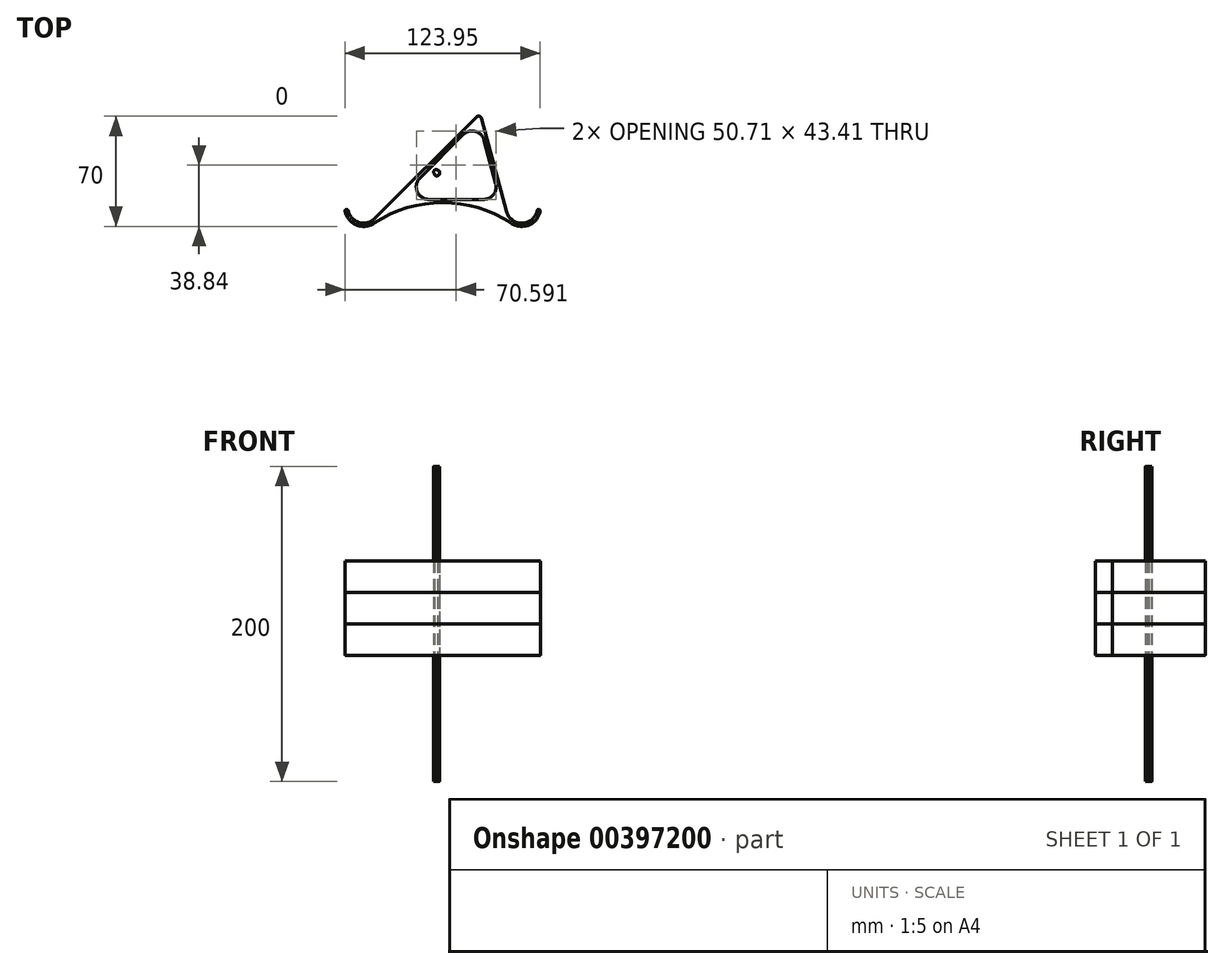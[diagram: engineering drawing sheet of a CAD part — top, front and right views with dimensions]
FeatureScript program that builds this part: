
annotation { "Feature Type Name" : "Feature", "Feature Type Description" : "" }
export const myFeature = defineFeature(function(context is Context, id is Id, definition is map)
    precondition{}
    {
        {
            var Q0;
            Q0=qCreatedBy(makeId("Top.planeOp"),FACE);
            var sketch = newSketch(context, id + "F0", { "sketchPlane" : qUnion([Q0])});
            skArc(sketch, "E0", {"start": v(-45.66, 8) * mm, "mid": v(-38.74, 0.42) * mm, "end": v(-28.8, 2.93) * mm});
            skArc(sketch, "E1.0", {"start": v(-47.62, 7.6) * mm, "mid": v(-39.32, -1.5) * mm, "end": v(-27.38, 1.51) * mm});
            skArc(sketch, "E2", {"start": v(-47.62, 7.6) * mm, "mid": v(-46.84, 8.78) * mm, "end": v(-45.66, 8) * mm});
            skArc(sketch, "E3.MirrorCS", {"start": v(76.3, 7.6) * mm, "mid": v(64.9, -2) * mm, "end": v(52.95, 6.9) * mm});
            skArc(sketch, "E4.MirrorCS", {"start": v(74.33, 8) * mm, "mid": v(64.84, 0) * mm, "end": v(54.88, 7.41) * mm});
            skLineSegment(sketch, "E5", {"start": v(-52.75, -2) * mm, "end": v(95.87, -2) * mm, "construction": true});
            skLineSegment(sketch, "E6", {"start": v(-28.8, 2.93) * mm, "end": v(35.7, 67.41) * mm});
            skLineSegment(sketch, "E7", {"start": v(54.88, 7.41) * mm, "end": v(39.04, 66.52) * mm});
            skLineSegment(sketch, "E8", {"start": v(52.95, 6.9) * mm, "end": v(40.7, 52.62) * mm});
            skLineSegment(sketch, "E9", {"start": v(-27.38, 1.51) * mm, "end": v(27.3, 56.2) * mm});
            skArc(sketch, "E10", {"start": v(74.33, 8) * mm, "mid": v(75.51, 8.78) * mm, "end": v(76.3, 7.6) * mm});
            skLineSegment(sketch, "E11", {"start": v(-7.94, 68) * mm, "end": v(55.98, 68) * mm, "construction": true});
            skArc(sketch, "E12", {"start": v(27.3, 56.2) * mm, "mid": v(35.04, 58.27) * mm, "end": v(40.7, 52.62) * mm});
            skArc(sketch, "E13", {"start": v(35.7, 67.41) * mm, "mid": v(37.63, 67.93) * mm, "end": v(39.04, 66.52) * mm});
            skArc(sketch, "E14", {"start": v(-0.1, 28.8) * mm, "mid": v(-1.83, 20.07) * mm, "end": v(5.56, 15.14) * mm});
            skArc(sketch, "E15", {"start": v(40.31, 15.14) * mm, "mid": v(46.66, 18.27) * mm, "end": v(48.04, 25.2) * mm});
            skArc(sketch, "E16", {"start": v(57.9, 0) * mm, "mid": v(14.34, 13.14) * mm, "end": v(-29.23, 0) * mm});
            skLineSegment(sketch, "E17", {"start": v(5.56, 15.14) * mm, "end": v(40.31, 15.14) * mm});
            skLineSegment(sketch, "E18", {"start": v(-34.41, 13.14) * mm, "end": v(67.53, 13.14) * mm, "construction": true});
            skLineSegment(sketch, "E19", {"start": v(5.56, 23.14) * mm, "end": v(32.97, 50.55) * mm, "construction": true});
            skLineSegment(sketch, "E20", {"start": v(40.31, 23.14) * mm, "end": v(5.56, 23.14) * mm, "construction": true});
            skLineSegment(sketch, "E21", {"start": v(32.97, 50.55) * mm, "end": v(40.31, 23.14) * mm, "construction": true});
            skLineSegment(sketch, "E22", {"start": v(5.56, 23.14) * mm, "end": v(36.64, 36.84) * mm, "construction": true});
            skLineSegment(sketch, "E23", {"start": v(36.64, 36.84) * mm, "end": v(40.31, 23.14) * mm, "construction": true});
            skLineSegment(sketch, "E24", {"start": v(40.31, 23.14) * mm, "end": v(19.26, 36.84) * mm, "construction": true});
            skLineSegment(sketch, "E25", {"start": v(19.26, 36.84) * mm, "end": v(32.97, 50.55) * mm, "construction": true});
            skLineSegment(sketch, "E26", {"start": v(32.97, 50.55) * mm, "end": v(22.93, 23.14) * mm, "construction": true});
            skLineSegment(sketch, "E27", {"start": v(26.28, 32.27) * mm, "end": v(26.28, 43.86) * mm, "construction": true});
            skSolve(sketch);
        }
        {
            var Q0;
            {var subQ3=sQuery(id+"F0.wireOp",EDGE,"E14");Q0=makeQuery(id+"F0.imprint","IMPRINT",FACE,{"disambiguationData":[TD([[makeQuery(id+"F0.imprint","IMPRINT",EDGE,{"derivedFrom":subQ3}),-1.0]])]});}
            var Q1;
            {var subQ5=sQuery(id+"F0.wireOp",EDGE,"E15");Q1=makeQuery(id+"F0.imprint","IMPRINT",FACE,{"disambiguationData":[TD([[makeQuery(id+"F0.imprint","IMPRINT",EDGE,{"derivedFrom":subQ5}),-1.0]])]});}
            var Q2;
            Q2=makeQuery(id+"F0.imprint","IMPRINT",FACE,{"disambiguationData":[TD([[makeQuery(id+"F0.imprint","IMPRINT",EDGE,{"derivedFrom":sQuery(id+"F0.wireOp",EDGE,"E0")}),-1.0]])]});
            extrude(context, id + "F1", {"entities" : qUnion([Q0, Q1, Q2]), "depth" : 40 * mm});
        }
        {
            var Q0;
            Q0=qCreatedBy(makeId("Top.planeOp"),FACE);
            var sketch = newSketch(context, id + "F2", { "sketchPlane" : qUnion([Q0])});
            skLineSegment(sketch, "E28.MirrorCS", {"start": v(6.62, 25.43) * mm, "end": v(6.62, 25.43) * mm});
            skLineSegment(sketch, "E29.MirrorCS", {"start": v(48.04, 35.28) * mm, "end": v(48.18, 35.73) * mm});
            skLineSegment(sketch, "E30.MirrorCS", {"start": v(49.9, 35.51) * mm, "end": v(50.43, 35.53) * mm});
            skFitSpline(sketch, "E31.MirrorCS", {"points": [v(50.57, 35.24) * mm, v(50.73, 34.92) * mm, v(50.74, 34.93) * mm, v(49.87, 34.77) * mm]});
            skLineSegment(sketch, "E32.MirrorCS", {"start": v(48.18, 35.73) * mm, "end": v(48.77, 35.62) * mm});
            skFitSpline(sketch, "E33.MirrorCS", {"points": [v(48.77, 35.62) * mm, v(49.1, 35.55) * mm, v(49.6, 35.5) * mm, v(49.9, 35.51) * mm]});
            skFitSpline(sketch, "E34.MirrorCS", {"points": [v(49.87, 34.77) * mm, v(49.4, 34.68) * mm, v(48.44, 34.7) * mm, v(48.06, 34.8) * mm]});
            skLineSegment(sketch, "E35.MirrorCS", {"start": v(45.66, 35.67) * mm, "end": v(46.15, 36.02) * mm});
            skLineSegment(sketch, "E36.MirrorCS", {"start": v(50.57, 35.24) * mm, "end": v(49.9, 35.51) * mm});
            skLineSegment(sketch, "E37.MirrorCS", {"start": v(48.77, 35.62) * mm, "end": v(48.04, 35.28) * mm});
            skLineSegment(sketch, "E38.MirrorCS", {"start": v(24.83, 34) * mm, "end": v(25.27, 33.6) * mm});
            skFitSpline(sketch, "E39.MirrorCS", {"points": [v(48.06, 34.8) * mm, v(47.93, 34.83) * mm, v(47.92, 34.91) * mm, v(48.04, 35.28) * mm]});
            skLineSegment(sketch, "E40.MirrorCS", {"start": v(50.43, 35.53) * mm, "end": v(50.57, 35.24) * mm});
            skLineSegment(sketch, "E41.MirrorCS", {"start": v(24.04, 33.1) * mm, "end": v(24.83, 34) * mm});
            skLineSegment(sketch, "E42.MirrorCS", {"start": v(27.95, 36.55) * mm, "end": v(27.5, 36.98) * mm});
            skLineSegment(sketch, "E43.MirrorCS", {"start": v(25.27, 33.6) * mm, "end": v(24.04, 33.1) * mm});
            skFitSpline(sketch, "E44.MirrorCS", {"points": [v(23.48, 31.83) * mm, v(23.32, 31.94) * mm, v(23.2, 32.08) * mm, v(23.22, 32.13) * mm]});
            skLineSegment(sketch, "E45.MirrorCS", {"start": v(45.99, 35.5) * mm, "end": v(45.66, 35.67) * mm});
            skFitSpline(sketch, "E46.MirrorCS", {"points": [v(9.41, 22.4) * mm, v(9.04, 22.05) * mm, v(8.66, 21.27) * mm, v(9.25, 20.95) * mm]});
            skFitSpline(sketch, "E47.MirrorCS", {"points": [v(42.3, 51.5) * mm, v(42.77, 51.58) * mm, v(43.01, 51.72) * mm, v(43.32, 52.05) * mm]});
            skFitSpline(sketch, "E48.MirrorCS", {"points": [v(31.88, 38.91) * mm, v(32.18, 39.25) * mm, v(32.3, 39.6) * mm, v(32.25, 40.03) * mm]});
            skFitSpline(sketch, "E49.MirrorCS", {"points": [v(30.97, 38.42) * mm, v(31.39, 38.5) * mm, v(31.6, 38.61) * mm, v(31.88, 38.91) * mm]});
            skFitSpline(sketch, "E50.MirrorCS", {"points": [v(23.05, 28.46) * mm, v(23.58, 28.75) * mm, v(24.07, 29.32) * mm, v(24.23, 29.83) * mm]});
            skFitSpline(sketch, "E51.MirrorCS", {"points": [v(26.76, 36.62) * mm, v(25.59, 36.98) * mm, v(24.53, 35.93) * mm, v(24.88, 34.73) * mm]});
            skFitSpline(sketch, "E52.MirrorCS", {"points": [v(28.34, 41.94) * mm, v(28.27, 41.8) * mm, v(28.2, 41.48) * mm, v(28.2, 41.21) * mm]});
            skLineSegment(sketch, "E53.MirrorCS", {"start": v(28.2, 40.72) * mm, "end": v(27.2, 39.57) * mm});
            skFitSpline(sketch, "E54.MirrorCS", {"points": [v(23.22, 32.13) * mm, v(23.24, 32.18) * mm, v(23.6, 32.62) * mm, v(24.04, 33.1) * mm]});
            skFitSpline(sketch, "E55.MirrorCS", {"points": [v(43.74, 53.32) * mm, v(43.67, 54.09) * mm, v(43.26, 54.6) * mm, v(42.55, 54.83) * mm]});
            skLineSegment(sketch, "E56.MirrorCS", {"start": v(27.2, 39.57) * mm, "end": v(28.2, 41.21) * mm});
            skLineSegment(sketch, "E57.MirrorCS", {"start": v(19.54, 31.48) * mm, "end": v(19.54, 30.95) * mm});
            skFitSpline(sketch, "E58.MirrorCS", {"points": [v(4.92, 38.14) * mm, v(5.34, 37.8) * mm, v(5.74, 37.41) * mm, v(5.81, 37.27) * mm]});
            skFitSpline(sketch, "E59.MirrorCS", {"points": [v(43.32, 52.05) * mm, v(43.66, 52.43) * mm, v(43.79, 52.83) * mm, v(43.74, 53.32) * mm]});
            skLineSegment(sketch, "E60.MirrorCS", {"start": v(28.2, 41.21) * mm, "end": v(28.2, 40.72) * mm});
            skFitSpline(sketch, "E61.MirrorCS", {"points": [v(22.21, 28.9) * mm, v(22.63, 28.97) * mm, v(22.84, 29.1) * mm, v(23.11, 29.4) * mm]});
            skLineSegment(sketch, "E62.MirrorCS", {"start": v(46.15, 36.02) * mm, "end": v(45.99, 35.5) * mm});
            skFitSpline(sketch, "E63.MirrorCS", {"points": [v(24.08, 37.14) * mm, v(23.93, 36.95) * mm, v(23.9, 36.8) * mm, v(23.9, 36.38) * mm]});
            skLineSegment(sketch, "E64.MirrorCS", {"start": v(22.89, 34.72) * mm, "end": v(23.9, 36.38) * mm});
            skLineSegment(sketch, "E65.MirrorCS", {"start": v(23.9, 36.38) * mm, "end": v(23.9, 35.86) * mm});
            skFitSpline(sketch, "E66.MirrorCS", {"points": [v(27.82, 40.9) * mm, v(27.75, 41.6) * mm, v(27.96, 42.45) * mm, v(28.7, 42.7) * mm]});
            skFitSpline(sketch, "E67.MirrorCS", {"points": [v(23.5, 30.51) * mm, v(23.43, 31.19) * mm, v(23.06, 31.65) * mm, v(22.43, 31.84) * mm]});
            skFitSpline(sketch, "E68.MirrorCS", {"points": [v(29.54, 42.54) * mm, v(29.08, 42.5) * mm, v(28.5, 42.2) * mm, v(28.34, 41.94) * mm]});
            skFitSpline(sketch, "E69.MirrorCS", {"points": [v(27.82, 35.29) * mm, v(27.76, 35.96) * mm, v(27.4, 36.42) * mm, v(26.76, 36.62) * mm]});
            skFitSpline(sketch, "E70.MirrorCS", {"points": [v(29.3, 39.47) * mm, v(29.5, 38.8) * mm, v(30.3, 38.3) * mm, v(30.97, 38.42) * mm]});
            skFitSpline(sketch, "E71.MirrorCS", {"points": [v(20.85, 32.83) * mm, v(19.99, 32.81) * mm, v(19.54, 32.35) * mm, v(19.54, 31.48) * mm]});
            skFitSpline(sketch, "E72.MirrorCS", {"points": [v(23.11, 29.4) * mm, v(23.41, 29.72) * mm, v(23.53, 30.08) * mm, v(23.5, 30.51) * mm]});
            skLineSegment(sketch, "E73.MirrorCS", {"start": v(27.5, 36.98) * mm, "end": v(28.26, 37.85) * mm});
            skFitSpline(sketch, "E74.MirrorCS", {"points": [v(22.89, 34.72) * mm, v(21.25, 32.86) * mm, v(21.22, 32.83) * mm, v(20.85, 32.83) * mm]});
            skFitSpline(sketch, "E75.MirrorCS", {"points": [v(46.22, 36.57) * mm, v(46.27, 36.55) * mm, v(46.24, 36.3) * mm, v(46.15, 36.02) * mm]});
            skFitSpline(sketch, "E76.MirrorCS", {"points": [v(19.15, 31.08) * mm, v(19.01, 31.98) * mm, v(19.48, 33.12) * mm, v(20.5, 33.17) * mm]});
            skFitSpline(sketch, "E77.MirrorCS", {"points": [v(53.13, 34.93) * mm, v(53.33, 34.16) * mm, v(52.73, 33.5) * mm, v(52.1, 33.16) * mm]});
            skLineSegment(sketch, "E78.MirrorCS", {"start": v(23.9, 35.86) * mm, "end": v(22.89, 34.72) * mm});
            skFitSpline(sketch, "E79.MirrorCS", {"points": [v(29.12, 38.78) * mm, v(29.18, 38.8) * mm, v(29.36, 38.7) * mm, v(29.52, 38.54) * mm]});
            skFitSpline(sketch, "E80.MirrorCS", {"points": [v(10.22, 20.85) * mm, v(9.4, 20.35) * mm, v(8.88, 20.44) * mm, v(8.6, 21.14) * mm]});
            skLineSegment(sketch, "E81.MirrorCS", {"start": v(28.26, 37.85) * mm, "end": v(27.95, 36.55) * mm});
            skFitSpline(sketch, "E82.MirrorCS", {"points": [v(28.26, 37.85) * mm, v(28.68, 38.33) * mm, v(29.07, 38.75) * mm, v(29.12, 38.78) * mm]});
            skFitSpline(sketch, "E83.MirrorCS", {"points": [v(22.43, 31.84) * mm, v(21.25, 32.2) * mm, v(20.2, 31.15) * mm, v(20.54, 29.95) * mm]});
            skFitSpline(sketch, "E84.MirrorCS", {"points": [v(32.25, 40.03) * mm, v(32.19, 40.71) * mm, v(31.82, 41.17) * mm, v(31.2, 41.36) * mm]});
            skFitSpline(sketch, "E85.MirrorCS", {"points": [v(5.76, 40.05) * mm, v(5.8, 40.08) * mm, v(6.57, 40.09) * mm, v(7.46, 40.07) * mm]});
            skFitSpline(sketch, "E86.MirrorCS", {"points": [v(24.23, 29.83) * mm, v(24.42, 30.47) * mm, v(24.09, 31.37) * mm, v(23.48, 31.83) * mm]});
            skFitSpline(sketch, "E87.MirrorCS", {"points": [v(6.18, 39.61) * mm, v(5.9, 39.83) * mm, v(5.7, 40.02) * mm, v(5.76, 40.05) * mm]});
            skFitSpline(sketch, "E88.MirrorCS", {"points": [v(24.88, 34.73) * mm, v(25.07, 34.06) * mm, v(25.88, 33.55) * mm, v(26.54, 33.67) * mm]});
            skFitSpline(sketch, "E89.MirrorCS", {"points": [v(27.2, 39.57) * mm, v(25.6, 37.77) * mm, v(25.5, 37.68) * mm, v(25.11, 37.67) * mm]});
            skFitSpline(sketch, "E90.MirrorCS", {"points": [v(32.14, 41.57) * mm, v(31.95, 41.73) * mm, v(31.82, 41.89) * mm, v(31.86, 41.92) * mm]});
            skFitSpline(sketch, "E91.MirrorCS", {"points": [v(20.43, 29) * mm, v(20.52, 29.09) * mm, v(20.6, 29.05) * mm, v(20.84, 28.82) * mm]});
            skFitSpline(sketch, "E92.MirrorCS", {"points": [v(31.2, 41.36) * mm, v(30.02, 41.73) * mm, v(28.96, 40.67) * mm, v(29.3, 39.47) * mm]});
            skFitSpline(sketch, "E93.MirrorCS", {"points": [v(22, 34.29) * mm, v(22.49, 34.87) * mm, v(23.05, 35.44) * mm, v(23.5, 36.04) * mm]});
            skFitSpline(sketch, "E94.MirrorCS", {"points": [v(52.54, 34.03) * mm, v(52.9, 34.47) * mm, v(52.88, 34.61) * mm, v(52.39, 35.88) * mm]});
            skFitSpline(sketch, "E95.MirrorCS", {"points": [v(3.58, 40.91) * mm, v(3.44, 40.63) * mm, v(3.42, 40.46) * mm, v(3.49, 40.06) * mm]});
            skFitSpline(sketch, "E96.MirrorCS", {"points": [v(3.49, 40.06) * mm, v(3.6, 39.4) * mm, v(4, 38.87) * mm, v(4.92, 38.14) * mm]});
            skFitSpline(sketch, "E97.MirrorCS", {"points": [v(28.52, 34.7) * mm, v(28.68, 35.22) * mm, v(28.68, 35.36) * mm, v(28.55, 35.72) * mm]});
            skFitSpline(sketch, "E98.MirrorCS", {"points": [v(28.55, 35.72) * mm, v(28.47, 35.95) * mm, v(28.21, 36.3) * mm, v(27.95, 36.55) * mm]});
            skFitSpline(sketch, "E99.MirrorCS", {"points": [v(25.69, 38.48) * mm, v(26.41, 39.27) * mm, v(27.16, 40.08) * mm, v(27.82, 40.9) * mm]});
            skFitSpline(sketch, "E100.MirrorCS", {"points": [v(20.5, 33.17) * mm, v(21.24, 33.1) * mm, v(21.53, 33.88) * mm, v(22, 34.29) * mm]});
            skFitSpline(sketch, "E101.MirrorCS", {"points": [v(5.06, 37.51) * mm, v(4.2, 38.24) * mm, v(3.1, 39.04) * mm, v(3.06, 40.28) * mm]});
            skFitSpline(sketch, "E102.MirrorCS", {"points": [v(48.78, 32.8) * mm, v(50.3, 32.7) * mm, v(51.92, 33.24) * mm, v(52.54, 34.03) * mm]});
            skFitSpline(sketch, "E103.MirrorCS", {"points": [v(44.95, 33.86) * mm, v(45.76, 33.42) * mm, v(47.79, 32.85) * mm, v(48.78, 32.8) * mm]});
            skFitSpline(sketch, "E104.MirrorCS", {"points": [v(40.4, 41.91) * mm, v(40.43, 41.9) * mm, v(40.56, 41.37) * mm, v(40.69, 40.73) * mm]});
            skFitSpline(sketch, "E105.MirrorCS", {"points": [v(40.4, 55.54) * mm, v(41.14, 56.15) * mm, v(42.13, 56.4) * mm, v(43, 56.12) * mm]});
            skFitSpline(sketch, "E106.MirrorCS", {"points": [v(44.8, 47.35) * mm, v(44.32, 49.01) * mm, v(43.4, 50.3) * mm, v(42.18, 50.97) * mm]});
            skFitSpline(sketch, "E107.MirrorCS", {"points": [v(45.58, 43.37) * mm, v(45.28, 45.13) * mm, v(44.93, 46.92) * mm, v(44.8, 47.35) * mm]});
            skFitSpline(sketch, "E108.MirrorCS", {"points": [v(25.11, 37.67) * mm, v(24.71, 37.67) * mm, v(24.34, 37.47) * mm, v(24.08, 37.14) * mm]});
            skFitSpline(sketch, "E109.MirrorCS", {"points": [v(20.38, 37.88) * mm, v(21.86, 38.76) * mm, v(22.27, 39.13) * mm, v(22.47, 39.77) * mm]});
            skFitSpline(sketch, "E110.MirrorCS", {"points": [v(41.42, 37.18) * mm, v(40.8, 38.4) * mm, v(40.46, 39.87) * mm, v(40.18, 41.1) * mm]});
            skFitSpline(sketch, "E111.MirrorCS", {"points": [v(39.23, 53.73) * mm, v(39.43, 54.38) * mm, v(39.84, 55.08) * mm, v(40.4, 55.54) * mm]});
            skFitSpline(sketch, "E112.MirrorCS", {"points": [v(7.88, 37.1) * mm, v(7.7, 38.16) * mm, v(7.28, 38.78) * mm, v(6.18, 39.61) * mm]});
            skFitSpline(sketch, "E113.MirrorCS", {"points": [v(20.84, 28.82) * mm, v(21.55, 28.13) * mm, v(22.26, 28.02) * mm, v(23.05, 28.46) * mm]});
            skFitSpline(sketch, "E114.MirrorCS", {"points": [v(17.8, 33.88) * mm, v(18.86, 36.74) * mm, v(19.1, 37.11) * mm, v(20.38, 37.88) * mm]});
            skFitSpline(sketch, "E115.MirrorCS", {"points": [v(39.39, 51.6) * mm, v(39.07, 52.27) * mm, v(39.01, 53.03) * mm, v(39.23, 53.73) * mm]});
            skFitSpline(sketch, "E116.MirrorCS", {"points": [v(19.37, 18.24) * mm, v(19.01, 17.77) * mm, v(18.31, 16.96) * mm, v(17.82, 16.45) * mm]});
            skFitSpline(sketch, "E117.MirrorCS", {"points": [v(22.62, 39.19) * mm, v(21.76, 37.77) * mm, v(19.66, 37.59) * mm, v(19.06, 35.94) * mm]});
            skFitSpline(sketch, "E118.MirrorCS", {"points": [v(0.36, 15) * mm, v(1.45, 13.37) * mm, v(2.47, 12.45) * mm, v(4.04, 11.65) * mm]});
            skFitSpline(sketch, "E119.MirrorCS", {"points": [v(10.96, 30.2) * mm, v(11.44, 30.3) * mm, v(11.7, 30.43) * mm, v(12, 30.78) * mm]});
            skFitSpline(sketch, "E120.MirrorCS", {"points": [v(17.64, 40.03) * mm, v(18.97, 40.04) * mm, v(20.07, 40.02) * mm, v(20.09, 40) * mm]});
            skFitSpline(sketch, "E121.MirrorCS", {"points": [v(40.69, 40.73) * mm, v(40.98, 39.23) * mm, v(41.28, 38.33) * mm, v(41.86, 37.18) * mm]});
            skFitSpline(sketch, "E122.MirrorCS", {"points": [v(2.49, 12.14) * mm, v(0.56, 13.59) * mm, v(-0.73, 15.73) * mm, v(-1.63, 17.93) * mm]});
            skFitSpline(sketch, "E123.MirrorCS", {"points": [v(19.56, 15.48) * mm, v(19.97, 15.92) * mm, v(21.03, 17.22) * mm, v(21.9, 18.36) * mm]});
            skFitSpline(sketch, "E124.MirrorCS", {"points": [v(5.58, 35.66) * mm, v(5.62, 36.31) * mm, v(5.67, 37.1) * mm, v(5.06, 37.51) * mm]});
            skFitSpline(sketch, "E125.MirrorCS", {"points": [v(6.62, 25.43) * mm, v(8.06, 25.42) * mm, v(8.9, 27.19) * mm, v(8, 28.3) * mm]});
            skFitSpline(sketch, "E126.MirrorCS", {"points": [v(4.75, 13.44) * mm, v(3.58, 14.04) * mm, v(2.93, 14.64) * mm, v(2.1, 15.87) * mm]});
            skFitSpline(sketch, "E127.MirrorCS", {"points": [v(9.02, 31.43) * mm, v(9.25, 30.66) * mm, v(10.18, 30.06) * mm, v(10.96, 30.2) * mm]});
            skFitSpline(sketch, "E128.MirrorCS", {"points": [v(43.53, 50.41) * mm, v(44.57, 49.35) * mm, v(45.18, 47.85) * mm, v(45.41, 46.4) * mm]});
            skFitSpline(sketch, "E129.MirrorCS", {"points": [v(5, 41.9) * mm, v(4.38, 41.79) * mm, v(3.82, 41.4) * mm, v(3.58, 40.91) * mm]});
            skFitSpline(sketch, "E130.MirrorCS", {"points": [v(40.23, 41.78) * mm, v(40.29, 41.87) * mm, v(40.36, 41.92) * mm, v(40.4, 41.91) * mm]});
            skFitSpline(sketch, "E131.MirrorCS", {"points": [v(24.55, 37.96) * mm, v(24.97, 38.05) * mm, v(25.45, 38.05) * mm, v(25.69, 38.48) * mm]});
            skFitSpline(sketch, "E132.MirrorCS", {"points": [v(39.56, 51.24) * mm, v(38.85, 51.13) * mm, v(38.46, 51) * mm, v(37.69, 50.59) * mm]});
            skFitSpline(sketch, "E133.MirrorCS", {"points": [v(20.09, 40) * mm, v(20.1, 39.97) * mm, v(19.75, 39.74) * mm, v(19.31, 39.48) * mm]});
            skFitSpline(sketch, "E134.MirrorCS", {"points": [v(12, 30.78) * mm, v(12.36, 31.17) * mm, v(12.5, 31.58) * mm, v(12.45, 32.08) * mm]});
            skFitSpline(sketch, "E135.MirrorCS", {"points": [v(25.27, 33.6) * mm, v(26.44, 32.56) * mm, v(28.02, 33.09) * mm, v(28.52, 34.7) * mm]});
            skFitSpline(sketch, "E136.MirrorCS", {"points": [v(44.98, 37.99) * mm, v(45.34, 37.35) * mm, v(45.95, 36.65) * mm, v(46.22, 36.57) * mm]});
            skFitSpline(sketch, "E137.MirrorCS", {"points": [v(23.5, 36.04) * mm, v(23.38, 36.82) * mm, v(23.74, 37.72) * mm, v(24.55, 37.96) * mm]});
            skFitSpline(sketch, "E138.MirrorCS", {"points": [v(21.83, 41.95) * mm, v(22.87, 41.5) * mm, v(23.25, 40.12) * mm, v(22.62, 39.19) * mm]});
            skFitSpline(sketch, "E139.MirrorCS", {"points": [v(40.41, 52.69) * mm, v(40.63, 51.94) * mm, v(41.54, 51.36) * mm, v(42.3, 51.5) * mm]});
            skFitSpline(sketch, "E140.MirrorCS", {"points": [v(-1.58, 21.03) * mm, v(-1.78, 19) * mm, v(-1.27, 17.42) * mm, v(0.36, 15) * mm]});
            skFitSpline(sketch, "E141.MirrorCS", {"points": [v(52.39, 35.88) * mm, v(51.8, 37.4) * mm, v(51.51, 37.66) * mm, v(50.65, 37.51) * mm]});
            skFitSpline(sketch, "E142.MirrorCS", {"points": [v(50.65, 37.51) * mm, v(49.94, 37.4) * mm, v(48.97, 37.5) * mm, v(48.11, 37.82) * mm]});
            skFitSpline(sketch, "E143.MirrorCS", {"points": [v(22.47, 39.77) * mm, v(22.7, 40.54) * mm, v(22.36, 41.27) * mm, v(21.59, 41.65) * mm]});
            skFitSpline(sketch, "E144.MirrorCS", {"points": [v(9.25, 20.95) * mm, v(10.07, 20.9) * mm, v(10.63, 21.73) * mm, v(11.18, 22.22) * mm]});
            skFitSpline(sketch, "E145.MirrorCS", {"points": [v(44.8, 54.16) * mm, v(45.03, 53.45) * mm, v(44.98, 52.68) * mm, v(44.77, 52) * mm]});
            skFitSpline(sketch, "E146.MirrorCS", {"points": [v(12.45, 32.08) * mm, v(12.37, 32.87) * mm, v(11.95, 33.4) * mm, v(11.22, 33.63) * mm]});
            skFitSpline(sketch, "E147.MirrorCS", {"points": [v(42.55, 54.83) * mm, v(41.22, 55.24) * mm, v(40.02, 54.04) * mm, v(40.41, 52.69) * mm]});
            skFitSpline(sketch, "E148.MirrorCS", {"points": [v(49.98, 37.84) * mm, v(50.69, 37.93) * mm, v(51.59, 38.1) * mm, v(52.05, 37.4) * mm]});
            skFitSpline(sketch, "E149.MirrorCS", {"points": [v(3.06, 40.28) * mm, v(3.02, 41.5) * mm, v(4.26, 42.3) * mm, v(5.37, 42.33) * mm]});
            skFitSpline(sketch, "E150.MirrorCS", {"points": [v(5.13, 28.15) * mm, v(4.87, 27.76) * mm, v(4.87, 27.73) * mm, v(4.85, 27.27) * mm]});
            skFitSpline(sketch, "E151.MirrorCS", {"points": [v(6.64, 21.04) * mm, v(6.77, 20.22) * mm, v(7.13, 19.6) * mm, v(7.76, 19.11) * mm]});
            skFitSpline(sketch, "E152.MirrorCS", {"points": [v(37.69, 50.59) * mm, v(36.8, 50.11) * mm, v(36.62, 49.97) * mm, v(35.44, 48.75) * mm]});
            skFitSpline(sketch, "E153.MirrorCS", {"points": [v(20.54, 29.95) * mm, v(20.74, 29.29) * mm, v(21.54, 28.77) * mm, v(22.21, 28.9) * mm]});
            skFitSpline(sketch, "E154.MirrorCS", {"points": [v(6.83, 22.51) * mm, v(6.55, 21.76) * mm, v(6.54, 21.68) * mm, v(6.64, 21.04) * mm]});
            skFitSpline(sketch, "E155.MirrorCS", {"points": [v(45.66, 35.67) * mm, v(45.06, 35.96) * mm, v(44.21, 36.87) * mm, v(43.73, 37.73) * mm]});
            skFitSpline(sketch, "E156.MirrorCS", {"points": [v(42.18, 50.97) * mm, v(41.52, 51.34) * mm, v(40.74, 51.42) * mm, v(39.56, 51.24) * mm]});
            skFitSpline(sketch, "E157.MirrorCS", {"points": [v(41.63, 44.26) * mm, v(41.04, 44.83) * mm, v(40.1, 44.66) * mm, v(39.41, 43.86) * mm]});
            skFitSpline(sketch, "E158.MirrorCS", {"points": [v(28.7, 42.7) * mm, v(29.16, 42.9) * mm, v(29.75, 42.87) * mm, v(30.01, 43.37) * mm]});
            skFitSpline(sketch, "E159.MirrorCS", {"points": [v(0.7, 22.62) * mm, v(1.06, 23.9) * mm, v(1.15, 24.14) * mm, v(1.54, 24.78) * mm]});
            skFitSpline(sketch, "E160.MirrorCS", {"points": [v(4.85, 27.27) * mm, v(4.82, 26.3) * mm, v(5.64, 25.44) * mm, v(6.62, 25.43) * mm]});
            skFitSpline(sketch, "E161.MirrorCS", {"points": [v(8.6, 21.14) * mm, v(8.35, 21.82) * mm, v(8.8, 22.49) * mm, v(10.64, 24.14) * mm]});
            skFitSpline(sketch, "E162.MirrorCS", {"points": [v(42.5, 41.56) * mm, v(42.13, 43.55) * mm, v(42.03, 43.87) * mm, v(41.63, 44.26) * mm]});
            skFitSpline(sketch, "E163.MirrorCS", {"points": [v(8, 28.3) * mm, v(7.24, 29.23) * mm, v(5.77, 29.15) * mm, v(5.13, 28.15) * mm]});
            skFitSpline(sketch, "E164.MirrorCS", {"points": [v(5.81, 37.27) * mm, v(6.1, 36.7) * mm, v(6.03, 35.3) * mm, v(5.66, 34.13) * mm]});
            skFitSpline(sketch, "E165.MirrorCS", {"points": [v(47, 39.1) * mm, v(47.64, 38.12) * mm, v(48.92, 37.93) * mm, v(49.98, 37.84) * mm]});
            skFitSpline(sketch, "E166.MirrorCS", {"points": [v(32.4, 38.69) * mm, v(33.24, 39.62) * mm, v(33.15, 40.69) * mm, v(32.14, 41.57) * mm]});
            skFitSpline(sketch, "E167.MirrorCS", {"points": [v(29.52, 38.54) * mm, v(30.44, 37.64) * mm, v(31.49, 37.7) * mm, v(32.4, 38.69) * mm]});
            skFitSpline(sketch, "E168.MirrorCS", {"points": [v(27.45, 34.17) * mm, v(27.75, 34.5) * mm, v(27.87, 34.85) * mm, v(27.82, 35.29) * mm]});
            skFitSpline(sketch, "E169.MirrorCS", {"points": [v(32.01, 45) * mm, v(30.08, 42.82) * mm, v(29.82, 42.56) * mm, v(29.54, 42.54) * mm]});
            skFitSpline(sketch, "E170.MirrorCS", {"points": [v(26.54, 33.67) * mm, v(26.96, 33.75) * mm, v(27.18, 33.87) * mm, v(27.45, 34.17) * mm]});
            skFitSpline(sketch, "E171.MirrorCS", {"points": [v(44.77, 52) * mm, v(44.56, 51.35) * mm, v(44.12, 50.78) * mm, v(43.53, 50.41) * mm]});
            skFitSpline(sketch, "E172.MirrorCS", {"points": [v(52.05, 37.4) * mm, v(52.6, 36.68) * mm, v(52.82, 35.77) * mm, v(53.13, 34.93) * mm]});
            skFitSpline(sketch, "E173.MirrorCS", {"points": [v(43, 56.12) * mm, v(43.86, 55.85) * mm, v(44.53, 55.06) * mm, v(44.8, 54.16) * mm]});
            skFitSpline(sketch, "E174.MirrorCS", {"points": [v(36.65, 50.41) * mm, v(37.46, 50.99) * mm, v(38.4, 51.42) * mm, v(39.39, 51.6) * mm]});
            skFitSpline(sketch, "E175.MirrorCS", {"points": [v(52.1, 33.16) * mm, v(50.18, 31.99) * mm, v(47.8, 32.36) * mm, v(45.8, 33.08) * mm]});
            skFitSpline(sketch, "E176.MirrorCS", {"points": [v(9.07, 41.98) * mm, v(7.12, 42) * mm, v(5.3, 41.97) * mm, v(5, 41.9) * mm]});
            skFitSpline(sketch, "E177.MirrorCS", {"points": [v(35.44, 48.75) * mm, v(34.74, 48.03) * mm, v(33.2, 46.34) * mm, v(32.01, 45) * mm]});
            skFitSpline(sketch, "E178.MirrorCS", {"points": [v(21.59, 41.65) * mm, v(21.04, 41.9) * mm, v(19.98, 41.97) * mm, v(16.13, 41.96) * mm]});
            skFitSpline(sketch, "E179.MirrorCS", {"points": [v(36.7, 36.66) * mm, v(31.22, 29.7) * mm, v(25.8, 22.7) * mm, v(20.3, 15.74) * mm]});
            skFitSpline(sketch, "E180.MirrorCS", {"points": [v(37.71, 48.32) * mm, v(39.2, 49.54) * mm, v(40.89, 49.74) * mm, v(41.9, 48.83) * mm]});
            skFitSpline(sketch, "E181.MirrorCS", {"points": [v(40.18, 41.1) * mm, v(39.07, 39.6) * mm, v(37.84, 38.16) * mm, v(36.7, 36.66) * mm]});
            skFitSpline(sketch, "E182.MirrorCS", {"points": [v(15.62, 28.86) * mm, v(13.87, 26.42) * mm, v(11.52, 24.5) * mm, v(9.41, 22.4) * mm]});
            skFitSpline(sketch, "E183.MirrorCS", {"points": [v(7.5, 10.42) * mm, v(11.54, 9.7) * mm, v(15.93, 11.53) * mm, v(19.56, 15.48) * mm]});
            skFitSpline(sketch, "E184.MirrorCS", {"points": [v(48.11, 37.82) * mm, v(46.6, 38.37) * mm, v(46.35, 38.9) * mm, v(45.58, 43.37) * mm]});
            skFitSpline(sketch, "E185.MirrorCS", {"points": [v(34.51, 44.9) * mm, v(35.94, 46.51) * mm, v(37.38, 48.05) * mm, v(37.71, 48.32) * mm]});
            skFitSpline(sketch, "E186.MirrorCS", {"points": [v(8.02, 12.28) * mm, v(7.27, 12.39) * mm, v(5.74, 12.93) * mm, v(4.75, 13.44) * mm]});
            skFitSpline(sketch, "E187.MirrorCS", {"points": [v(19.06, 35.94) * mm, v(18, 33.55) * mm, v(17.34, 30.9) * mm, v(15.62, 28.86) * mm]});
            skFitSpline(sketch, "E188.MirrorCS", {"points": [v(31.86, 41.92) * mm, v(31.89, 41.95) * mm, v(33.08, 43.29) * mm, v(34.51, 44.9) * mm]});
            skFitSpline(sketch, "E189.MirrorCS", {"points": [v(17.82, 16.45) * mm, v(14.66, 13.2) * mm, v(11.34, 11.79) * mm, v(8.02, 12.28) * mm]});
            skFitSpline(sketch, "E190.MirrorCS", {"points": [v(4.04, 11.65) * mm, v(5.03, 11.14) * mm, v(6.62, 10.58) * mm, v(7.5, 10.42) * mm]});
            skFitSpline(sketch, "E191.MirrorCS", {"points": [v(45.8, 33.08) * mm, v(43.82, 33.73) * mm, v(42.28, 35.32) * mm, v(41.42, 37.18) * mm]});
            skFitSpline(sketch, "E192.MirrorCS", {"points": [v(6.83, 32) * mm, v(7.62, 33.33) * mm, v(8.11, 35.71) * mm, v(7.88, 37.1) * mm]});
            skFitSpline(sketch, "E193.MirrorCS", {"points": [v(15.58, 29.47) * mm, v(16.58, 30.84) * mm, v(16.96, 31.6) * mm, v(17.8, 33.88) * mm]});
            skFitSpline(sketch, "E194.MirrorCS", {"points": [v(16.13, 41.96) * mm, v(14.18, 41.96) * mm, v(11, 41.97) * mm, v(9.07, 41.98) * mm]});
            skFitSpline(sketch, "E195.MirrorCS", {"points": [v(43.65, 43.19) * mm, v(44.17, 39.96) * mm, v(44.42, 38.97) * mm, v(44.98, 37.99) * mm]});
            skFitSpline(sketch, "E196.MirrorCS", {"points": [v(41.86, 37.18) * mm, v(42.64, 35.63) * mm, v(43.57, 34.63) * mm, v(44.95, 33.86) * mm]});
            skFitSpline(sketch, "E197.MirrorCS", {"points": [v(21.9, 18.36) * mm, v(23.77, 20.79) * mm, v(31.12, 30.18) * mm, v(36.43, 36.93) * mm]});
            skFitSpline(sketch, "E198.MirrorCS", {"points": [v(45.41, 46.4) * mm, v(45.97, 43.97) * mm, v(46.09, 41.42) * mm, v(47, 39.1) * mm]});
            skFitSpline(sketch, "E199.MirrorCS", {"points": [v(9.25, 25.48) * mm, v(7.53, 23.95) * mm, v(7.21, 23.55) * mm, v(6.83, 22.51) * mm]});
            skFitSpline(sketch, "E200.MirrorCS", {"points": [v(36.43, 36.93) * mm, v(38.47, 39.52) * mm, v(40.18, 41.7) * mm, v(40.23, 41.78) * mm]});
            skFitSpline(sketch, "E201.MirrorCS", {"points": [v(19.31, 39.48) * mm, v(17.62, 38.5) * mm, v(16.89, 37.4) * mm, v(15.98, 34.48) * mm]});
            skLineSegment(sketch, "E202.MirrorCS", {"start": v(19.54, 30.95) * mm, "end": v(15.78, 26.72) * mm});
            skLineSegment(sketch, "E203.MirrorCS", {"start": v(15.78, 26.72) * mm, "end": v(19.54, 31.48) * mm});
            skFitSpline(sketch, "E204.MirrorCS", {"points": [v(41.9, 48.83) * mm, v(42.7, 48.1) * mm, v(43.05, 46.96) * mm, v(43.65, 43.19) * mm]});
            skFitSpline(sketch, "E205.MirrorCS", {"points": [v(2.1, 15.87) * mm, v(1.26, 17.13) * mm, v(0.55, 18.5) * mm, v(0.4, 19.19) * mm]});
            skFitSpline(sketch, "E206.MirrorCS", {"points": [v(14.44, 31.18) * mm, v(13.2, 29.34) * mm, v(11.6, 27.57) * mm, v(9.25, 25.48) * mm]});
            skFitSpline(sketch, "E207.MirrorCS", {"points": [v(9.7, 9.88) * mm, v(7.13, 9.8) * mm, v(4.6, 10.72) * mm, v(2.49, 12.14) * mm]});
            skFitSpline(sketch, "E208.MirrorCS", {"points": [v(11.18, 22.22) * mm, v(13.93, 25.1) * mm, v(16.48, 28.14) * mm, v(19.15, 31.08) * mm]});
            skFitSpline(sketch, "E209.MirrorCS", {"points": [v(2.68, 30.2) * mm, v(3.9, 31.86) * mm, v(5.45, 33.5) * mm, v(5.58, 35.66) * mm]});
            skFitSpline(sketch, "E210.MirrorCS", {"points": [v(-0.99, 24.87) * mm, v(-0.07, 26.83) * mm, v(1.38, 28.48) * mm, v(2.68, 30.2) * mm]});
            skFitSpline(sketch, "E211.MirrorCS", {"points": [v(4.06, 28.2) * mm, v(5.44, 29.93) * mm, v(6.33, 31.15) * mm, v(6.83, 32) * mm]});
            skFitSpline(sketch, "E212.MirrorCS", {"points": [v(7.46, 40.07) * mm, v(9.39, 40.04) * mm, v(14.3, 40.02) * mm, v(17.64, 40.03) * mm]});
            skFitSpline(sketch, "E213.MirrorCS", {"points": [v(11.22, 33.63) * mm, v(9.85, 34.06) * mm, v(8.62, 32.82) * mm, v(9.02, 31.43) * mm]});
            skFitSpline(sketch, "E214.MirrorCS", {"points": [v(20.3, 15.74) * mm, v(17.64, 12.6) * mm, v(13.9, 10.1) * mm, v(9.7, 9.88) * mm]});
            skFitSpline(sketch, "E215.MirrorCS", {"points": [v(-1.63, 17.93) * mm, v(-2.4, 20.22) * mm, v(-1.84, 22.7) * mm, v(-0.99, 24.87) * mm]});
            skFitSpline(sketch, "E216.MirrorCS", {"points": [v(15.98, 34.48) * mm, v(15.54, 33.08) * mm, v(15.15, 32.24) * mm, v(14.44, 31.18) * mm]});
            skFitSpline(sketch, "E217.MirrorCS", {"points": [v(5.66, 34.13) * mm, v(5.38, 33.21) * mm, v(4.8, 32.3) * mm, v(3.27, 30.34) * mm]});
            skFitSpline(sketch, "E218.MirrorCS", {"points": [v(0.4, 19.19) * mm, v(0.19, 20.07) * mm, v(0.28, 21.04) * mm, v(0.7, 22.62) * mm]});
            skFitSpline(sketch, "E219.MirrorCS", {"points": [v(15.78, 26.72) * mm, v(11.5, 21.9) * mm, v(10.9, 21.26) * mm, v(10.22, 20.85) * mm]});
            skFitSpline(sketch, "E220.MirrorCS", {"points": [v(7.76, 19.11) * mm, v(8.92, 18.2) * mm, v(10.6, 18.51) * mm, v(12.2, 19.91) * mm]});
            skFitSpline(sketch, "E221.MirrorCS", {"points": [v(-0.5, 25.04) * mm, v(-0.93, 24.11) * mm, v(-1.47, 22.14) * mm, v(-1.58, 21.03) * mm]});
            skFitSpline(sketch, "E222.MirrorCS", {"points": [v(39.41, 43.86) * mm, v(39.03, 43.41) * mm, v(20.32, 19.5) * mm, v(19.37, 18.24) * mm]});
            skFitSpline(sketch, "E223.MirrorCS", {"points": [v(16.55, 24.67) * mm, v(18.62, 27) * mm, v(20.36, 28.95) * mm, v(20.43, 29) * mm]});
            skFitSpline(sketch, "E224.MirrorCS", {"points": [v(10.64, 24.14) * mm, v(12.9, 26.18) * mm, v(14.21, 27.58) * mm, v(15.58, 29.47) * mm]});
            skFitSpline(sketch, "E225.MirrorCS", {"points": [v(17.52, 42.34) * mm, v(18.95, 42.23) * mm, v(20.47, 42.53) * mm, v(21.83, 41.95) * mm]});
            skFitSpline(sketch, "E226.MirrorCS", {"points": [v(30.01, 43.37) * mm, v(32.24, 45.7) * mm, v(34.22, 48.3) * mm, v(36.65, 50.41) * mm]});
            skFitSpline(sketch, "E227.MirrorCS", {"points": [v(12.2, 19.91) * mm, v(12.53, 20.2) * mm, v(14.49, 22.34) * mm, v(16.55, 24.67) * mm]});
            skFitSpline(sketch, "E228.MirrorCS", {"points": [v(1.54, 24.78) * mm, v(2.08, 25.65) * mm, v(2.85, 26.7) * mm, v(4.06, 28.2) * mm]});
            skFitSpline(sketch, "E229.MirrorCS", {"points": [v(5.37, 42.33) * mm, v(9.42, 42.4) * mm, v(13.47, 42.34) * mm, v(17.52, 42.34) * mm]});
            skFitSpline(sketch, "E230.MirrorCS", {"points": [v(3.27, 30.34) * mm, v(1.25, 27.78) * mm, v(-0.1, 25.86) * mm, v(-0.5, 25.04) * mm]});
            skFitSpline(sketch, "E231.MirrorCS", {"points": [v(43.73, 37.73) * mm, v(43.13, 38.79) * mm, v(42.89, 39.55) * mm, v(42.5, 41.56) * mm]});
            skSolve(sketch);
        }
        {
            var Q0;
            Q0=makeQuery(id+"F2.imprint","IMPRINT",FACE,{"disambiguationData":[TD([[makeQuery(id+"F2.imprint","IMPRINT",EDGE,{"derivedFrom":sQuery(id+"F2.wireOp",EDGE,"E119.MirrorCS")}),1.0]])]});
            var Q1;
            Q1=makeQuery(id+"F2.imprint","IMPRINT",FACE,{"disambiguationData":[TD([[makeQuery(id+"F2.imprint","IMPRINT",EDGE,{"derivedFrom":sQuery(id+"F2.wireOp",EDGE,"E29.MirrorCS")}),1.0]])]});
            var Q2;
            Q2=makeQuery(id+"F2.imprint","IMPRINT",FACE,{"disambiguationData":[TD([[makeQuery(id+"F2.imprint","IMPRINT",EDGE,{"derivedFrom":sQuery(id+"F2.wireOp",EDGE,"E48.MirrorCS")}),1.0]])]});
            var Q3;
            Q3=makeQuery(id+"F2.imprint","IMPRINT",FACE,{"disambiguationData":[TD([[makeQuery(id+"F2.imprint","IMPRINT",EDGE,{"derivedFrom":sQuery(id+"F2.wireOp",EDGE,"E61.MirrorCS")}),1.0]])]});
            var Q4;
            Q4=makeQuery(id+"F2.imprint","IMPRINT",FACE,{"disambiguationData":[TD([[makeQuery(id+"F2.imprint","IMPRINT",EDGE,{"derivedFrom":sQuery(id+"F2.wireOp",EDGE,"E51.MirrorCS")}),1.0]])]});
            var Q5;
            Q5=makeQuery(id+"F2.imprint","IMPRINT",FACE,{"disambiguationData":[TD([[makeQuery(id+"F2.imprint","IMPRINT",EDGE,{"derivedFrom":sQuery(id+"F2.wireOp",EDGE,"E28.MirrorCS")}),-1.0]])]});
            var Q6;
            Q6=makeQuery(id+"F2.imprint","IMPRINT",FACE,{"disambiguationData":[TD([[makeQuery(id+"F2.imprint","IMPRINT",EDGE,{"derivedFrom":sQuery(id+"F2.wireOp",EDGE,"E28.MirrorCS")}),1.0]])]});
            var Q7;
            Q7=makeQuery(id+"F2.imprint","IMPRINT",FACE,{"disambiguationData":[TD([[makeQuery(id+"F2.imprint","IMPRINT",EDGE,{"derivedFrom":sQuery(id+"F2.wireOp",EDGE,"E57.MirrorCS")}),-1.0]])]});
            var Q8;
            Q8=makeQuery(id+"F2.imprint","IMPRINT",FACE,{"disambiguationData":[TD([[makeQuery(id+"F2.imprint","IMPRINT",EDGE,{"derivedFrom":sQuery(id+"F2.wireOp",EDGE,"E31.MirrorCS")}),-1.0]])]});
            var Q9;
            Q9=makeQuery(id+"F2.imprint","IMPRINT",FACE,{"disambiguationData":[TD([[makeQuery(id+"F2.imprint","IMPRINT",EDGE,{"derivedFrom":sQuery(id+"F2.wireOp",EDGE,"E64.MirrorCS")}),-1.0]])]});
            var Q10;
            Q10=makeQuery(id+"F2.imprint","IMPRINT",FACE,{"disambiguationData":[TD([[makeQuery(id+"F2.imprint","IMPRINT",EDGE,{"derivedFrom":sQuery(id+"F2.wireOp",EDGE,"E38.MirrorCS")}),-1.0]])]});
            var Q11;
            Q11=makeQuery(id+"F2.imprint","IMPRINT",FACE,{"disambiguationData":[TD([[makeQuery(id+"F2.imprint","IMPRINT",EDGE,{"derivedFrom":sQuery(id+"F2.wireOp",EDGE,"E42.MirrorCS")}),-1.0]])]});
            var Q12;
            Q12=makeQuery(id+"F2.imprint","IMPRINT",FACE,{"disambiguationData":[TD([[makeQuery(id+"F2.imprint","IMPRINT",EDGE,{"derivedFrom":sQuery(id+"F2.wireOp",EDGE,"E53.MirrorCS")}),-1.0]])]});
            var Q13;
            Q13=makeQuery(id+"F2.imprint","IMPRINT",FACE,{"disambiguationData":[TD([[makeQuery(id+"F2.imprint","IMPRINT",EDGE,{"derivedFrom":sQuery(id+"F2.wireOp",EDGE,"E29.MirrorCS")}),-1.0]])]});
            var Q14;
            Q14=makeQuery(id+"F2.imprint","IMPRINT",FACE,{"disambiguationData":[TD([[makeQuery(id+"F2.imprint","IMPRINT",EDGE,{"derivedFrom":sQuery(id+"F2.wireOp",EDGE,"E30.MirrorCS")}),-1.0]])]});
            var Q15;
            Q15=makeQuery(id+"F2.imprint","IMPRINT",FACE,{"disambiguationData":[TD([[makeQuery(id+"F2.imprint","IMPRINT",EDGE,{"derivedFrom":sQuery(id+"F2.wireOp",EDGE,"E35.MirrorCS")}),-1.0]])]});
            extrude(context, id + "F3", {"entities" : qUnion([Q0, Q1, Q2, Q3, Q4, Q5, Q6, Q7, Q8, Q9, Q10, Q11, Q12, Q13, Q14, Q15]), "endBound" : BoundingType.SYMMETRIC, "depth" : 200 * mm});
        }
        {
            var Q0;
            Q0=makeQuery(id+"F3.opExtrude","SWEPT_BODY",BODY,{"disambiguationData":[OSD([sQuery(id+"F2.wireOp",EDGE,"E52.MirrorCS"),sQuery(id+"F2.wireOp",EDGE,"E56.MirrorCS"),sQuery(id+"F2.wireOp",EDGE,"E58.MirrorCS"),sQuery(id+"F2.wireOp",EDGE,"E63.MirrorCS"),sQuery(id+"F2.wireOp",EDGE,"E64.MirrorCS"),sQuery(id+"F2.wireOp",EDGE,"E68.MirrorCS"),sQuery(id+"F2.wireOp",EDGE,"E71.MirrorCS"),sQuery(id+"F2.wireOp",EDGE,"E74.MirrorCS"),sQuery(id+"F2.wireOp",EDGE,"E80.MirrorCS"),sQuery(id+"F2.wireOp",EDGE,"E89.MirrorCS"),sQuery(id+"F2.wireOp",EDGE,"E94.MirrorCS"),sQuery(id+"F2.wireOp",EDGE,"E95.MirrorCS"),sQuery(id+"F2.wireOp",EDGE,"E96.MirrorCS"),sQuery(id+"F2.wireOp",EDGE,"E102.MirrorCS"),sQuery(id+"F2.wireOp",EDGE,"E103.MirrorCS"),sQuery(id+"F2.wireOp",EDGE,"E104.MirrorCS"),sQuery(id+"F2.wireOp",EDGE,"E106.MirrorCS"),sQuery(id+"F2.wireOp",EDGE,"E107.MirrorCS"),sQuery(id+"F2.wireOp",EDGE,"E108.MirrorCS"),sQuery(id+"F2.wireOp",EDGE,"E109.MirrorCS"),sQuery(id+"F2.wireOp",EDGE,"E114.MirrorCS"),sQuery(id+"F2.wireOp",EDGE,"E118.MirrorCS"),sQuery(id+"F2.wireOp",EDGE,"E121.MirrorCS"),sQuery(id+"F2.wireOp",EDGE,"E123.MirrorCS"),sQuery(id+"F2.wireOp",EDGE,"E129.MirrorCS"),sQuery(id+"F2.wireOp",EDGE,"E130.MirrorCS"),sQuery(id+"F2.wireOp",EDGE,"E132.MirrorCS"),sQuery(id+"F2.wireOp",EDGE,"E140.MirrorCS"),sQuery(id+"F2.wireOp",EDGE,"E141.MirrorCS"),sQuery(id+"F2.wireOp",EDGE,"E142.MirrorCS"),sQuery(id+"F2.wireOp",EDGE,"E143.MirrorCS"),sQuery(id+"F2.wireOp",EDGE,"E152.MirrorCS"),sQuery(id+"F2.wireOp",EDGE,"E156.MirrorCS"),sQuery(id+"F2.wireOp",EDGE,"E161.MirrorCS"),sQuery(id+"F2.wireOp",EDGE,"E164.MirrorCS"),sQuery(id+"F2.wireOp",EDGE,"E169.MirrorCS"),sQuery(id+"F2.wireOp",EDGE,"E176.MirrorCS"),sQuery(id+"F2.wireOp",EDGE,"E177.MirrorCS"),sQuery(id+"F2.wireOp",EDGE,"E178.MirrorCS"),sQuery(id+"F2.wireOp",EDGE,"E183.MirrorCS"),sQuery(id+"F2.wireOp",EDGE,"E184.MirrorCS"),sQuery(id+"F2.wireOp",EDGE,"E190.MirrorCS"),sQuery(id+"F2.wireOp",EDGE,"E193.MirrorCS"),sQuery(id+"F2.wireOp",EDGE,"E194.MirrorCS"),sQuery(id+"F2.wireOp",EDGE,"E196.MirrorCS"),sQuery(id+"F2.wireOp",EDGE,"E197.MirrorCS"),sQuery(id+"F2.wireOp",EDGE,"E200.MirrorCS"),sQuery(id+"F2.wireOp",EDGE,"E203.MirrorCS"),sQuery(id+"F2.wireOp",EDGE,"E217.MirrorCS"),sQuery(id+"F2.wireOp",EDGE,"E219.MirrorCS"),sQuery(id+"F2.wireOp",EDGE,"E221.MirrorCS"),sQuery(id+"F2.wireOp",EDGE,"E224.MirrorCS"),sQuery(id+"F2.wireOp",EDGE,"E230.MirrorCS")])]});
            var Q1;
            Q1=sQuery(id+"F0.wireOp",VERTEX,"E27.start");
            transform(context, id + "F4", {"entities" : qUnion([Q0]), "transformType" : TransformType.SCALE_UNIFORMLY, "scale" : 0.7, "scalePoint" : qUnion([Q1]), "makeCopy" : false});
        }
        {
            var Q0;
            Q0 = qSketchRegion(id + "F0", true);
            var Q1;
            {var subQ1=sQuery(id+"F0.wireOp",EDGE,"E12");Q1=makeQuery(id+"F0.imprint","IMPRINT",FACE,{"disambiguationData":[TD([[makeQuery(id+"F0.imprint","IMPRINT",EDGE,{"derivedFrom":subQ1}),-1.0]])]});}
            extrude(context, id + "F5", {"entities" : qUnion([Q0, Q1]), "endBound" : BoundingType.SYMMETRIC, "depth" : 40 * mm});
        }
        {
            var Q0;
            Q0=makeQuery(id+"F3.opExtrude","SWEPT_BODY",BODY,{"disambiguationData":[OSD([sQuery(id+"F2.wireOp",EDGE,"E52.MirrorCS"),sQuery(id+"F2.wireOp",EDGE,"E56.MirrorCS"),sQuery(id+"F2.wireOp",EDGE,"E58.MirrorCS"),sQuery(id+"F2.wireOp",EDGE,"E63.MirrorCS"),sQuery(id+"F2.wireOp",EDGE,"E64.MirrorCS"),sQuery(id+"F2.wireOp",EDGE,"E68.MirrorCS"),sQuery(id+"F2.wireOp",EDGE,"E71.MirrorCS"),sQuery(id+"F2.wireOp",EDGE,"E74.MirrorCS"),sQuery(id+"F2.wireOp",EDGE,"E80.MirrorCS"),sQuery(id+"F2.wireOp",EDGE,"E89.MirrorCS"),sQuery(id+"F2.wireOp",EDGE,"E94.MirrorCS"),sQuery(id+"F2.wireOp",EDGE,"E95.MirrorCS"),sQuery(id+"F2.wireOp",EDGE,"E96.MirrorCS"),sQuery(id+"F2.wireOp",EDGE,"E102.MirrorCS"),sQuery(id+"F2.wireOp",EDGE,"E103.MirrorCS"),sQuery(id+"F2.wireOp",EDGE,"E104.MirrorCS"),sQuery(id+"F2.wireOp",EDGE,"E106.MirrorCS"),sQuery(id+"F2.wireOp",EDGE,"E107.MirrorCS"),sQuery(id+"F2.wireOp",EDGE,"E108.MirrorCS"),sQuery(id+"F2.wireOp",EDGE,"E109.MirrorCS"),sQuery(id+"F2.wireOp",EDGE,"E114.MirrorCS"),sQuery(id+"F2.wireOp",EDGE,"E118.MirrorCS"),sQuery(id+"F2.wireOp",EDGE,"E121.MirrorCS"),sQuery(id+"F2.wireOp",EDGE,"E123.MirrorCS"),sQuery(id+"F2.wireOp",EDGE,"E129.MirrorCS"),sQuery(id+"F2.wireOp",EDGE,"E130.MirrorCS"),sQuery(id+"F2.wireOp",EDGE,"E132.MirrorCS"),sQuery(id+"F2.wireOp",EDGE,"E140.MirrorCS"),sQuery(id+"F2.wireOp",EDGE,"E141.MirrorCS"),sQuery(id+"F2.wireOp",EDGE,"E142.MirrorCS"),sQuery(id+"F2.wireOp",EDGE,"E143.MirrorCS"),sQuery(id+"F2.wireOp",EDGE,"E152.MirrorCS"),sQuery(id+"F2.wireOp",EDGE,"E156.MirrorCS"),sQuery(id+"F2.wireOp",EDGE,"E161.MirrorCS"),sQuery(id+"F2.wireOp",EDGE,"E164.MirrorCS"),sQuery(id+"F2.wireOp",EDGE,"E169.MirrorCS"),sQuery(id+"F2.wireOp",EDGE,"E176.MirrorCS"),sQuery(id+"F2.wireOp",EDGE,"E177.MirrorCS"),sQuery(id+"F2.wireOp",EDGE,"E178.MirrorCS"),sQuery(id+"F2.wireOp",EDGE,"E183.MirrorCS"),sQuery(id+"F2.wireOp",EDGE,"E184.MirrorCS"),sQuery(id+"F2.wireOp",EDGE,"E190.MirrorCS"),sQuery(id+"F2.wireOp",EDGE,"E193.MirrorCS"),sQuery(id+"F2.wireOp",EDGE,"E194.MirrorCS"),sQuery(id+"F2.wireOp",EDGE,"E196.MirrorCS"),sQuery(id+"F2.wireOp",EDGE,"E197.MirrorCS"),sQuery(id+"F2.wireOp",EDGE,"E200.MirrorCS"),sQuery(id+"F2.wireOp",EDGE,"E203.MirrorCS"),sQuery(id+"F2.wireOp",EDGE,"E217.MirrorCS"),sQuery(id+"F2.wireOp",EDGE,"E219.MirrorCS"),sQuery(id+"F2.wireOp",EDGE,"E221.MirrorCS"),sQuery(id+"F2.wireOp",EDGE,"E224.MirrorCS"),sQuery(id+"F2.wireOp",EDGE,"E230.MirrorCS")])]});
            var Q1;
            Q1=makeQuery(id+"F5.opExtrude","SWEPT_BODY",BODY,{"disambiguationData":[OSD([sQuery(id+"F0.wireOp",EDGE,"E0"),sQuery(id+"F0.wireOp",EDGE,"E1.0"),sQuery(id+"F0.wireOp",EDGE,"E2"),sQuery(id+"F0.wireOp",EDGE,"E3.MirrorCS"),sQuery(id+"F0.wireOp",EDGE,"E4.MirrorCS"),sQuery(id+"F0.wireOp",EDGE,"E6"),sQuery(id+"F0.wireOp",EDGE,"E7"),sQuery(id+"F0.wireOp",EDGE,"E10"),sQuery(id+"F0.wireOp",EDGE,"E13"),sQuery(id+"F0.wireOp",EDGE,"E16")])]});
            booleanBodies(context, id + "F6", {"operationType" : BooleanOperationType.SUBTRACTION, "tools" : qUnion([Q0]), "targets" : qUnion([Q1])});
        }
    });
